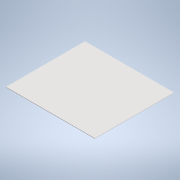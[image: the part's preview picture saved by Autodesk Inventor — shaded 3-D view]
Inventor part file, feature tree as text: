
AUTODESK INVENTOR PART (.ipt)
format: ipt  version: 2021 (Build 250183000, 183)  size: 120,320 bytes
history: native  units: mm
features: sketch x2, extrude x1, hole x1
ambient origin geometry x8: Origin, YZ Plane, XZ Plane, XY Plane, X Axis, Y Axis, Z Axis, Center Point
bodies: Solid1 (feature_tree)
feature tree (4):
  extrude  "base"  Depth=2200.0mm
  hole  "mountHoles"  [1 undecoded]
  sketch  "Sketch1"  dims[d0=1100.0mm d1=2200.0mm]
  sketch  "Sketch2"  dims[d2=1600.0mm d3=800.0mm d4=10.0mm d5=0.0mm d10=900.0mm d11=900.0mm d12=550.0mm d13=550.0mm d14=275.0mm d15=275.0mm d16=450.0mm d17=450.0mm d18=10.0mm d19=8.0mm d20=4.0mm d21=2.0mm d22=90.0deg d23=8.0mm d24=20.594885mm]
note: 1 required parameter value undecoded (feature->parameter linkage not recoverable at this tier; creation-order binding heuristic only, values carry confidence <= 0.55)
